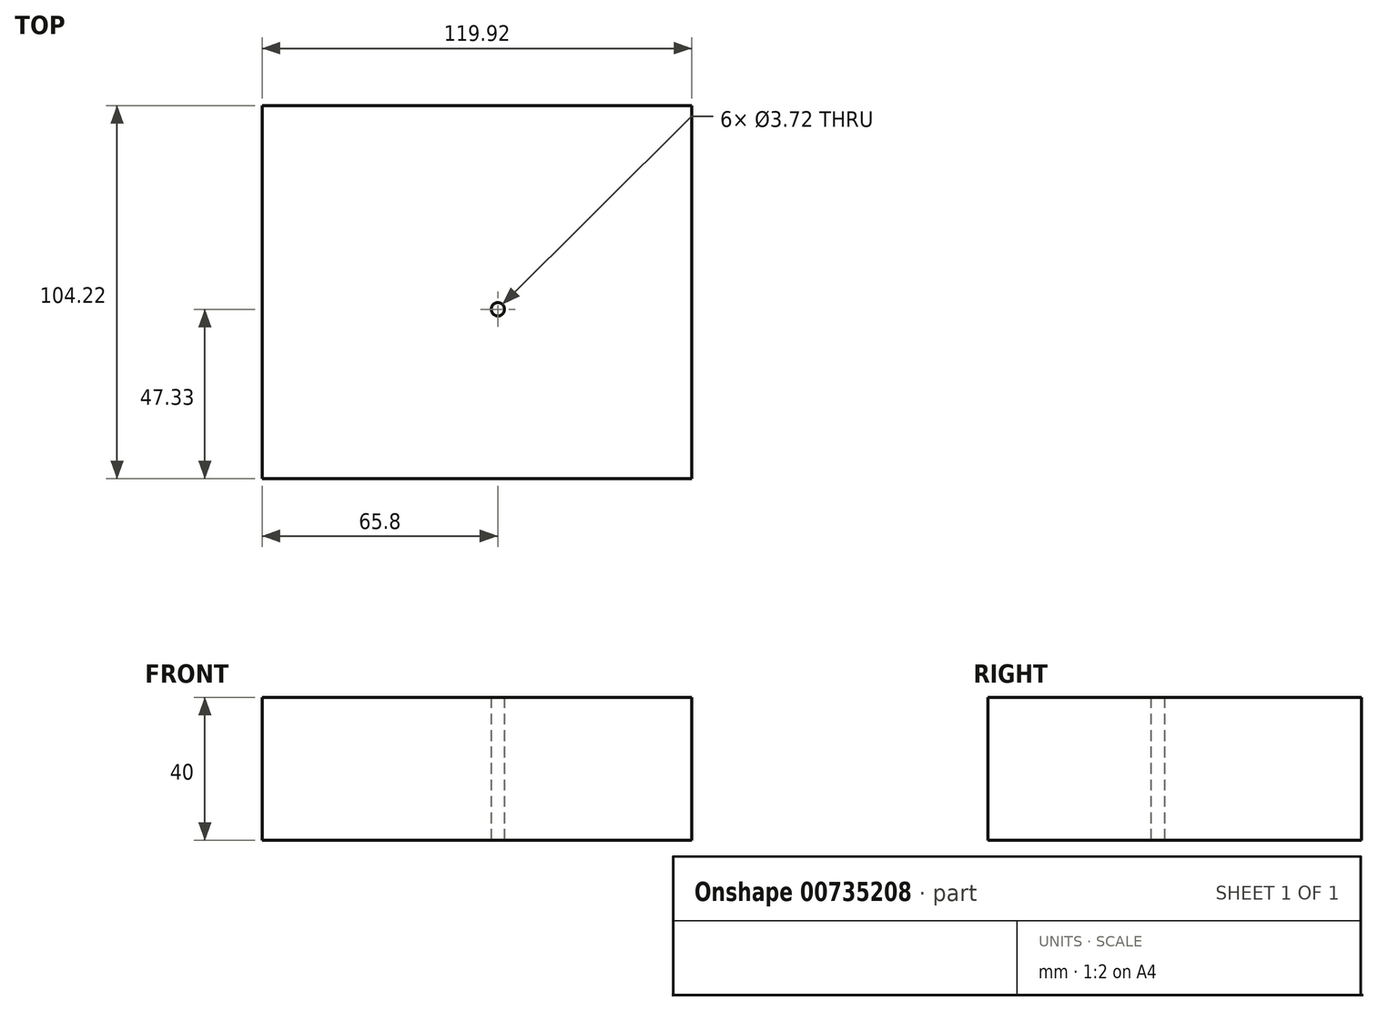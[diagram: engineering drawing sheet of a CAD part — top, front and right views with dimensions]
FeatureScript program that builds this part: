
annotation { "Feature Type Name" : "Feature", "Feature Type Description" : "" }
export const myFeature = defineFeature(function(context is Context, id is Id, definition is map)
    precondition{}
    {
        {
            var Q0;
            Q0=qCreatedBy(makeId("Top.planeOp"),FACE);
            var sketch = newSketch(context, id + "F0", { "sketchPlane" : qUnion([Q0])});
            skLineSegment(sketch, "E0.bottom", {"start": v(-65.8, -47.33) * mm, "end": v(54.12, -47.33) * mm});
            skLineSegment(sketch, "E0.top", {"start": v(-65.8, 56.89) * mm, "end": v(54.12, 56.89) * mm});
            skLineSegment(sketch, "E0.left", {"start": v(-65.8, -47.33) * mm, "end": v(-65.8, 56.89) * mm});
            skLineSegment(sketch, "E0.right", {"start": v(54.12, -47.33) * mm, "end": v(54.12, 56.89) * mm});
            skSolve(sketch);
        }
        {
            var Q0;
            Q0=makeQuery(id+"F0.imprint","IMPRINT",FACE,{"disambiguationData":[TD([[makeQuery(id+"F0.imprint","IMPRINT",EDGE,{"derivedFrom":sQuery(id+"F0.wireOp",EDGE,"E0.bottom")}),1.0]])]});
            extrude(context, id + "F1", {"entities" : qUnion([Q0]), "depth" : 40 * mm, "offsetDistance" : 25.4 * mm});
        }
        {
            var Q0;
            Q0=makeQuery(id+"F1.opExtrude","CAP_FACE",FACE,{"disambiguationData":[OSD([sQuery(id+"F0.wireOp",EDGE,"E0.bottom"),sQuery(id+"F0.wireOp",EDGE,"E0.top"),sQuery(id+"F0.wireOp",EDGE,"E0.left"),sQuery(id+"F0.wireOp",EDGE,"E0.right")])],"isStart":false});
            var sketch = newSketch(context, id + "F2", { "sketchPlane" : qUnion([Q0])});
            skCircle(sketch, "E1", {"center": v(0, 0) * mm, "radius": 1.86 * mm});
            skSolve(sketch);
        }
        {
            var Q0;
            Q0 = qSketchRegion(id + "F2", true);
            extrude(context, id + "F3", {"entities" : qUnion([Q0]), "operationType" : NewBodyOperationType.REMOVE, "depth" : 32 * mm, "offsetDistance" : 25.4 * mm, "hasSecondDirection" : true, "secondDirectionOppositeDirection" : true, "secondDirectionDepth" : 58.67 * mm});
        }
    });
